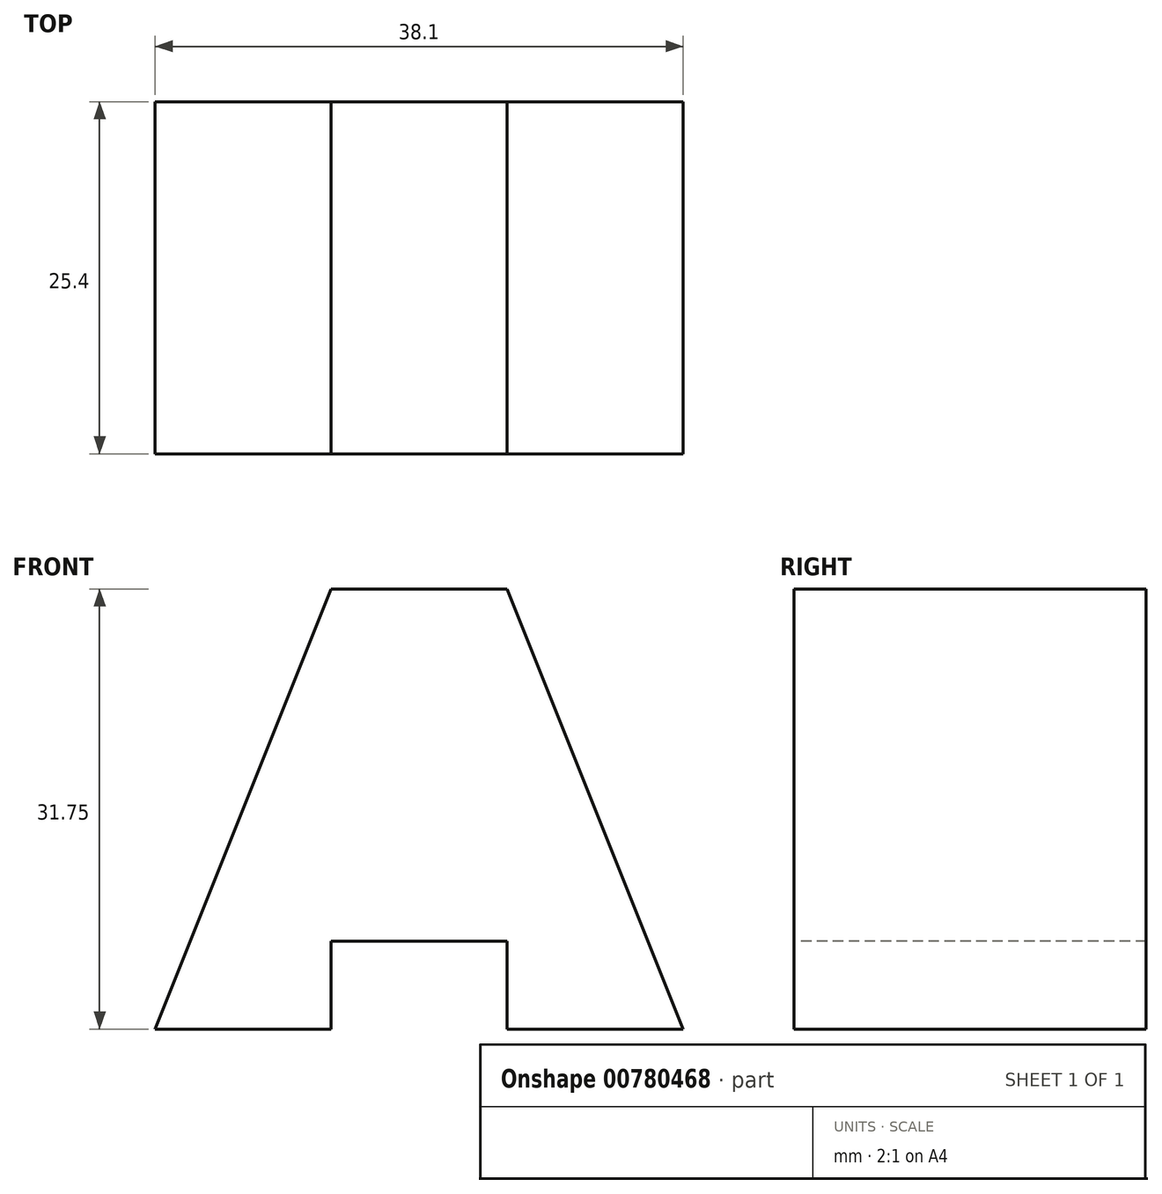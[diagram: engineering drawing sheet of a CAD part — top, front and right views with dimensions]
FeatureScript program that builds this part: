
annotation { "Feature Type Name" : "Feature", "Feature Type Description" : "" }
export const myFeature = defineFeature(function(context is Context, id is Id, definition is map)
    precondition{}
    {
        {
            var Q0;
            Q0=qCreatedBy(makeId("Front.planeOp"),FACE);
            var sketch = newSketch(context, id + "F0", { "sketchPlane" : qUnion([Q0])});
            skLineSegment(sketch, "E0", {"start": v(0, 0) * mm, "end": v(38.1, 0) * mm});
            skLineSegment(sketch, "E1", {"start": v(38.1, 0) * mm, "end": v(38.1, 31.75) * mm});
            skLineSegment(sketch, "E2", {"start": v(38.1, 31.75) * mm, "end": v(0, 31.75) * mm});
            skLineSegment(sketch, "E3", {"start": v(0, 31.75) * mm, "end": v(0, 0) * mm});
            skSolve(sketch);
        }
        {
            var Q0;
            Q0=makeQuery(id+"F0.imprint","IMPRINT",FACE,{"disambiguationData":[TD([[makeQuery(id+"F0.imprint","IMPRINT",EDGE,{"derivedFrom":sQuery(id+"F0.wireOp",EDGE,"E0")}),1.0]])]});
            extrude(context, id + "F1", {"entities" : qUnion([Q0]), "depth" : 25.4 * mm, "offsetDistance" : 25.4 * mm});
        }
        {
            var Q0;
            Q0=makeQuery(id+"F1.opExtrude","CAP_FACE",FACE,{"disambiguationData":[OSD([sQuery(id+"F0.wireOp",EDGE,"E0"),sQuery(id+"F0.wireOp",EDGE,"E1"),sQuery(id+"F0.wireOp",EDGE,"E2"),sQuery(id+"F0.wireOp",EDGE,"E3")])],"isStart":false});
            var sketch = newSketch(context, id + "F2", { "sketchPlane" : qUnion([Q0])});
            skLineSegment(sketch, "E4", {"start": v(0, 31.75) * mm, "end": v(12.7, 31.75) * mm});
            skLineSegment(sketch, "E5", {"start": v(38.1, 31.75) * mm, "end": v(25.4, 31.75) * mm});
            skLineSegment(sketch, "E6", {"start": v(0, 0) * mm, "end": v(12.7, 31.75) * mm});
            skLineSegment(sketch, "E7", {"start": v(38.1, 0) * mm, "end": v(25.4, 31.75) * mm});
            skLineSegment(sketch, "E8", {"start": v(25.4, 31.75) * mm, "end": v(12.7, 31.75) * mm});
            skSolve(sketch);
        }
        {
            var Q0;
            Q0=makeQuery(id+"F2.imprint","IMPRINT",FACE,{"disambiguationData":[TD([[makeQuery(id+"F2.imprint","IMPRINT",EDGE,{"derivedFrom":sQuery(id+"F2.wireOp",EDGE,"E5")}),1.0]])]});
            extrude(context, id + "F3", {"entities" : qUnion([Q0]), "operationType" : NewBodyOperationType.REMOVE, "oppositeDirection" : true, "depth" : 25.4 * mm, "offsetDistance" : 25.4 * mm});
        }
        {
            var Q0;
            Q0=makeQuery(id+"F2.imprint","IMPRINT",FACE,{"disambiguationData":[TD([[makeQuery(id+"F2.imprint","IMPRINT",EDGE,{"derivedFrom":sQuery(id+"F2.wireOp",EDGE,"E4")}),1.0]])]});
            extrude(context, id + "F4", {"entities" : qUnion([Q0]), "operationType" : NewBodyOperationType.REMOVE, "oppositeDirection" : true, "depth" : 25.4 * mm, "offsetDistance" : 25.4 * mm});
        }
        {
            var Q0;
            Q0=makeQuery(id+"F1.opExtrude","CAP_FACE",FACE,{"disambiguationData":[OSD([sQuery(id+"F0.wireOp",EDGE,"E0"),sQuery(id+"F0.wireOp",EDGE,"E1"),sQuery(id+"F0.wireOp",EDGE,"E2"),sQuery(id+"F0.wireOp",EDGE,"E3")])],"isStart":false});
            var sketch = newSketch(context, id + "F5", { "sketchPlane" : qUnion([Q0])});
            skLineSegment(sketch, "E9", {"start": v(0, 0) * mm, "end": v(12.7, 0) * mm});
            skLineSegment(sketch, "E10", {"start": v(38.1, 0) * mm, "end": v(25.4, 0) * mm});
            skLineSegment(sketch, "E11", {"start": v(12.7, 0) * mm, "end": v(12.7, 6.35) * mm});
            skLineSegment(sketch, "E12", {"start": v(25.4, 0) * mm, "end": v(25.4, 6.35) * mm});
            skLineSegment(sketch, "E13", {"start": v(12.7, 6.35) * mm, "end": v(25.4, 6.35) * mm});
            skSolve(sketch);
        }
        {
            var Q0;
            {var subQ0=sQuery(id+"F5.wireOp",EDGE,"E11");Q0=makeQuery(id+"F5.imprint","IMPRINT",FACE,{"disambiguationData":[TD([[makeQuery(id+"F5.imprint","IMPRINT",EDGE,{"derivedFrom":subQ0}),-1.0]])]});}
            extrude(context, id + "F6", {"entities" : qUnion([Q0]), "operationType" : NewBodyOperationType.REMOVE, "oppositeDirection" : true, "depth" : 25.4 * mm, "offsetDistance" : 25.4 * mm});
        }
    });
